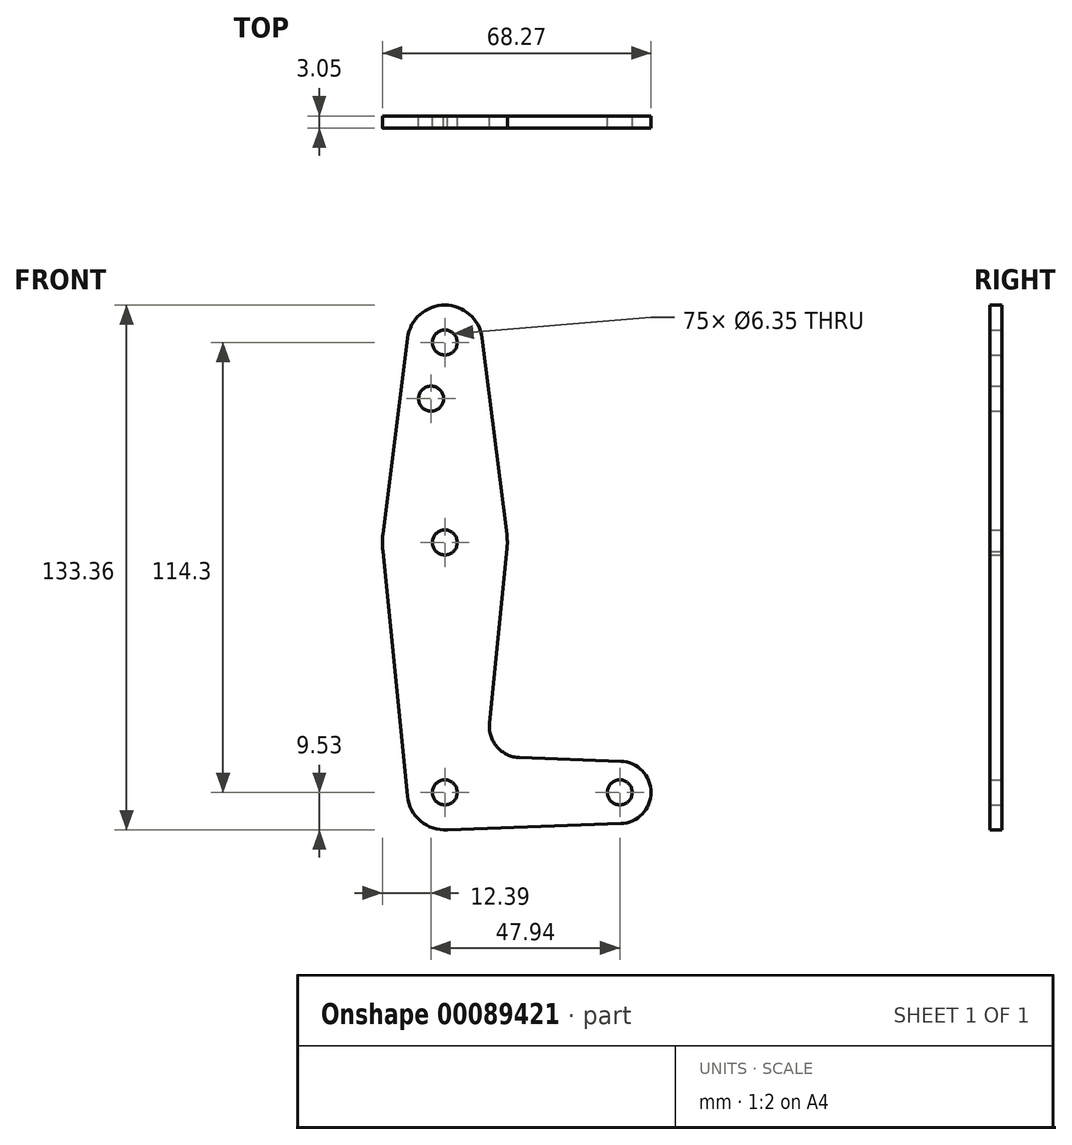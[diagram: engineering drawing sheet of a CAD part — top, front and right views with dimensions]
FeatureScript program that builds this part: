
annotation { "Feature Type Name" : "Feature", "Feature Type Description" : "" }
export const myFeature = defineFeature(function(context is Context, id is Id, definition is map)
    precondition{}
    {
        {
            var Q0;
            Q0=qCreatedBy(makeId("Front.planeOp"),FACE);
            var sketch = newSketch(context, id + "F0", { "sketchPlane" : qUnion([Q0])});
            skLineSegment(sketch, "E0", {"start": v(0, 114.3) * mm, "end": v(0, 0) * mm});
            skLineSegment(sketch, "E1", {"start": v(0, 0) * mm, "end": v(44.45, 0) * mm});
            skCircle(sketch, "E2", {"center": v(0, 114.3) * mm, "radius": 9.53 * mm});
            skCircle(sketch, "E3", {"center": v(0, 63.5) * mm, "radius": 15.88 * mm});
            skCircle(sketch, "E4", {"center": v(0, 0) * mm, "radius": 9.53 * mm});
            skCircle(sketch, "E5", {"center": v(44.45, 0) * mm, "radius": 7.94 * mm});
            skLineSegment(sketch, "E6", {"start": v(-9.45, 115.5) * mm, "end": v(-15.75, 65.48) * mm});
            skLineSegment(sketch, "E7", {"start": v(9.45, 115.5) * mm, "end": v(15.75, 65.48) * mm});
            skLineSegment(sketch, "E8", {"start": v(0, -9.53) * mm, "end": v(44.73, -7.93) * mm});
            skCircle(sketch, "E9", {"center": v(0, 114.3) * mm, "radius": 3.18 * mm});
            skCircle(sketch, "E10", {"center": v(0, 63.5) * mm, "radius": 3.18 * mm});
            skCircle(sketch, "E11", {"center": v(0, 0) * mm, "radius": 3.18 * mm});
            skCircle(sketch, "E12", {"center": v(44.45, 0) * mm, "radius": 3.18 * mm});
            skCircle(sketch, "E13", {"center": v(-3.49, 100.03) * mm, "radius": 3.18 * mm});
            skLineSegment(sketch, "E14", {"start": v(15.8, 61.91) * mm, "end": v(11.34, 17.59) * mm});
            skLineSegment(sketch, "E15", {"start": v(18.97, 8.85) * mm, "end": v(44.73, 7.93) * mm});
            skArc(sketch, "E16.filletArc", {"start": v(11.34, 17.59) * mm, "mid": v(13.26, 11.57) * mm, "end": v(18.97, 8.85) * mm});
            skLineSegment(sketch, "E17", {"start": v(-15.7, 61.2) * mm, "end": v(-9.48, -0.95) * mm});
            skSolve(sketch);
        }
        {
            var Q0;
            Q0 = qSketchRegion(id + "F0", true);
            var Q1;
            {var subQ0=sQuery(id+"F0.wireOp",EDGE,"E4");var subQ1=sQuery(id+"F0.wireOp",EDGE,"E0");var subQ2=makeQuery(id+"F0.imprint","INTERSECT",VERTEX,{"derivedFrom":[subQ1,subQ0]});Q1=makeQuery(id+"F0.imprint","IMPRINT",FACE,{"disambiguationData":[TD([[makeQuery(id+"F0.imprint","IMPRINT",EDGE,{"disambiguationData":[TD([[subQ2,-1.0]])],"derivedFrom":subQ1}),1.0]])]});}
            extrude(context, id + "F1", {"entities" : qUnion([Q0, Q1]), "depth" : 3.05 * mm});
        }
    });
